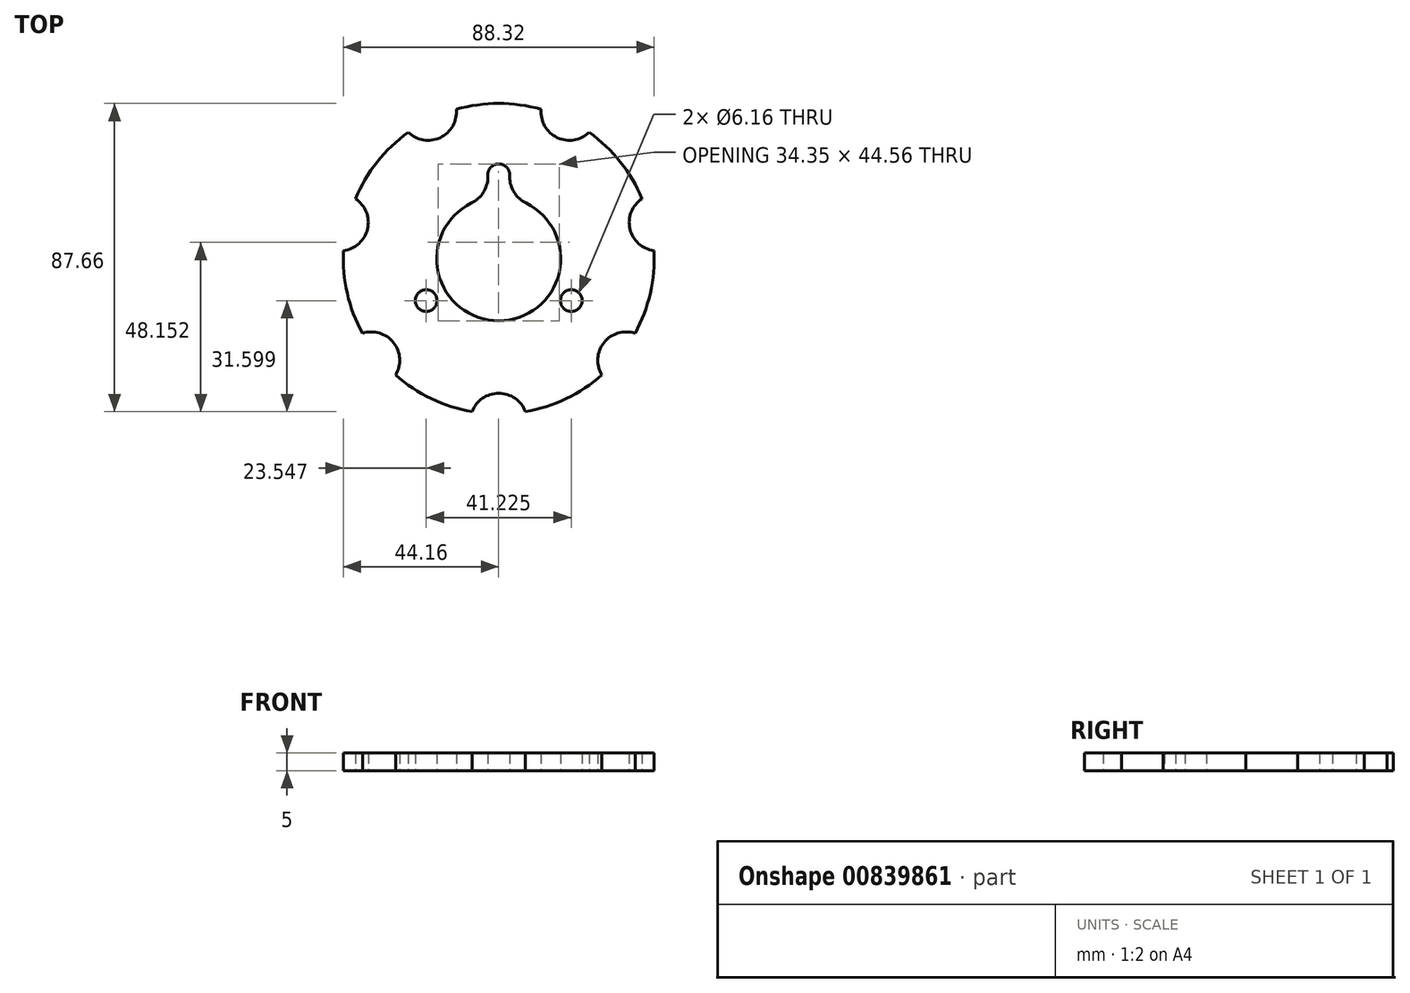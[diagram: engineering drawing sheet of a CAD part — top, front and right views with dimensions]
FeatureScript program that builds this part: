
annotation { "Feature Type Name" : "Feature", "Feature Type Description" : "" }
export const myFeature = defineFeature(function(context is Context, id is Id, definition is map)
    precondition{}
    {
        {
            var Q0;
            Q0=qCreatedBy(makeId("Top.planeOp"),FACE);
            var sketch = newSketch(context, id + "F0", { "sketchPlane" : qUnion([Q0])});
            skCircle(sketch, "E0", {"center": v(0, 0) * mm, "radius": 44.16 * mm});
            skCircle(sketch, "E1", {"center": v(0, 44.16) * mm, "radius": 12.16 * mm});
            skCircle(sketch, "E2.1.0", {"center": v(-34.52, 27.53) * mm, "radius": 12.16 * mm});
            skCircle(sketch, "E2.2.0", {"center": v(-43.05, -9.83) * mm, "radius": 12.16 * mm});
            skCircle(sketch, "E2.3.0", {"center": v(-19.16, -39.79) * mm, "radius": 12.16 * mm});
            skCircle(sketch, "E2.4.0", {"center": v(19.16, -39.79) * mm, "radius": 12.16 * mm});
            skCircle(sketch, "E2.5.0", {"center": v(43.05, -9.83) * mm, "radius": 12.16 * mm});
            skCircle(sketch, "E2.6.0", {"center": v(34.52, 27.53) * mm, "radius": 12.16 * mm});
            skCircle(sketch, "E3", {"center": v(20.1, 41.73) * mm, "radius": 8.08 * mm});
            skPoint(sketch, "E3.first.point", {"position": v(25.7, 35.9) * mm});
            skPoint(sketch, "E3.second.point", {"position": v(12.05, 42.48) * mm});
            skPoint(sketch, "E3.third.point", {"position": v(24.63, 48.42) * mm});
            skCircle(sketch, "E4.1.0", {"center": v(-20.1, 41.73) * mm, "radius": 8.08 * mm});
            skCircle(sketch, "E4.2.0", {"center": v(-45.16, 10.3) * mm, "radius": 8.08 * mm});
            skCircle(sketch, "E4.3.0", {"center": v(-36.21, -28.88) * mm, "radius": 8.08 * mm});
            skCircle(sketch, "E4.4.0", {"center": v(0, -46.32) * mm, "radius": 8.08 * mm});
            skCircle(sketch, "E4.5.0", {"center": v(36.21, -28.88) * mm, "radius": 8.08 * mm});
            skCircle(sketch, "E4.6.0", {"center": v(45.16, 10.3) * mm, "radius": 8.08 * mm});
            skCircle(sketch, "E5", {"center": v(0, 0) * mm, "radius": 17.63 * mm});
            skCircle(sketch, "E6", {"center": v(0, 23.8) * mm, "radius": 3.08 * mm});
            skCircle(sketch, "E7", {"center": v(0, 23.8) * mm, "radius": 3.13 * mm});
            skArc(sketch, "E8", {"start": v(-7.76, 15.83) * mm, "mid": v(-4.38, 18.85) * mm, "end": v(-3.07, 23.2) * mm});
            skArc(sketch, "E9.MirrorCS", {"start": v(7.76, 15.83) * mm, "mid": v(4.38, 18.85) * mm, "end": v(3.07, 23.2) * mm});
            skArc(sketch, "E10.1.0", {"start": v(-9.83, -14.64) * mm, "mid": v(-14.14, -13.22) * mm, "end": v(-18.55, -14.26) * mm});
            skCircle(sketch, "E10.1.1", {"center": v(-20.61, -11.9) * mm, "radius": 3.08 * mm});
            skArc(sketch, "E10.1.2", {"start": v(-17.59, -1.2) * mm, "mid": v(-18.52, -5.63) * mm, "end": v(-21.63, -8.94) * mm});
            skArc(sketch, "E10.2.0", {"start": v(17.59, -1.2) * mm, "mid": v(18.52, -5.63) * mm, "end": v(21.63, -8.94) * mm});
            skCircle(sketch, "E10.2.1", {"center": v(20.61, -11.9) * mm, "radius": 3.08 * mm});
            skArc(sketch, "E10.2.2", {"start": v(9.83, -14.64) * mm, "mid": v(14.14, -13.22) * mm, "end": v(18.55, -14.26) * mm});
            skSolve(sketch);
        }
        {
            var Q0;
            {var subQ1=sQuery(id+"F0.wireOp",EDGE,"E8");Q0=makeQuery(id+"F0.imprint","IMPRINT",FACE,{"disambiguationData":[TD([[makeQuery(id+"F0.imprint","IMPRINT",EDGE,{"derivedFrom":subQ1}),1.0]])]});}
            var Q1;
            {var subQ0=sQuery(id+"F0.wireOp",EDGE,"E2.1.0");var subQ1=sQuery(id+"F0.wireOp",EDGE,"E0");var subQ2=makeQuery(id+"F0.imprint","INTERSECT",VERTEX,{"derivedFrom":[subQ1,subQ0,sQuery(id+"F0.wireOp",EDGE,"E4.1.0")]});Q1=makeQuery(id+"F0.imprint","IMPRINT",FACE,{"disambiguationData":[TD([[makeQuery(id+"F0.imprint","IMPRINT",EDGE,{"disambiguationData":[TD([[subQ2,-1.0]])],"derivedFrom":subQ1}),1.0]])]});}
            var Q2;
            {var subQ0=sQuery(id+"F0.wireOp",EDGE,"E2.2.0");var subQ1=sQuery(id+"F0.wireOp",EDGE,"E0");var subQ2=makeQuery(id+"F0.imprint","INTERSECT",VERTEX,{"derivedFrom":[subQ1,subQ0,sQuery(id+"F0.wireOp",EDGE,"E4.2.0")]});Q2=makeQuery(id+"F0.imprint","IMPRINT",FACE,{"disambiguationData":[TD([[makeQuery(id+"F0.imprint","IMPRINT",EDGE,{"disambiguationData":[TD([[subQ2,-1.0]])],"derivedFrom":subQ1}),1.0]])]});}
            var Q3;
            {var subQ0=sQuery(id+"F0.wireOp",EDGE,"E2.3.0");var subQ1=sQuery(id+"F0.wireOp",EDGE,"E0");var subQ2=makeQuery(id+"F0.imprint","INTERSECT",VERTEX,{"derivedFrom":[subQ1,subQ0,sQuery(id+"F0.wireOp",EDGE,"E4.3.0")]});Q3=makeQuery(id+"F0.imprint","IMPRINT",FACE,{"disambiguationData":[TD([[makeQuery(id+"F0.imprint","IMPRINT",EDGE,{"disambiguationData":[TD([[subQ2,-1.0]])],"derivedFrom":subQ1}),1.0]])]});}
            var Q4;
            {var subQ0=sQuery(id+"F0.wireOp",EDGE,"E2.4.0");var subQ1=sQuery(id+"F0.wireOp",EDGE,"E0");var subQ2=makeQuery(id+"F0.imprint","INTERSECT",VERTEX,{"derivedFrom":[subQ1,subQ0,sQuery(id+"F0.wireOp",EDGE,"E4.4.0")]});Q4=makeQuery(id+"F0.imprint","IMPRINT",FACE,{"disambiguationData":[TD([[makeQuery(id+"F0.imprint","IMPRINT",EDGE,{"disambiguationData":[TD([[subQ2,-1.0]])],"derivedFrom":subQ1}),1.0]])]});}
            var Q5;
            {var subQ0=sQuery(id+"F0.wireOp",EDGE,"E2.5.0");var subQ1=sQuery(id+"F0.wireOp",EDGE,"E0");var subQ2=makeQuery(id+"F0.imprint","INTERSECT",VERTEX,{"derivedFrom":[subQ1,subQ0,sQuery(id+"F0.wireOp",EDGE,"E4.6.0")]});Q5=makeQuery(id+"F0.imprint","IMPRINT",FACE,{"disambiguationData":[TD([[makeQuery(id+"F0.imprint","IMPRINT",EDGE,{"disambiguationData":[TD([[subQ2,1.0]])],"derivedFrom":subQ1}),1.0]])]});}
            var Q6;
            {var subQ0=sQuery(id+"F0.wireOp",EDGE,"E2.6.0");var subQ1=sQuery(id+"F0.wireOp",EDGE,"E0");var subQ2=makeQuery(id+"F0.imprint","INTERSECT",VERTEX,{"derivedFrom":[subQ1,subQ0,sQuery(id+"F0.wireOp",EDGE,"E4.6.0")]});Q6=makeQuery(id+"F0.imprint","IMPRINT",FACE,{"disambiguationData":[TD([[makeQuery(id+"F0.imprint","IMPRINT",EDGE,{"disambiguationData":[TD([[subQ2,-1.0]])],"derivedFrom":subQ1}),1.0]])]});}
            var Q7;
            {var subQ0=sQuery(id+"F0.wireOp",EDGE,"E1");var subQ1=sQuery(id+"F0.wireOp",EDGE,"E0");var subQ2=makeQuery(id+"F0.imprint","INTERSECT",VERTEX,{"derivedFrom":[subQ1,subQ0,sQuery(id+"F0.wireOp",EDGE,"E3")]});Q7=makeQuery(id+"F0.imprint","IMPRINT",FACE,{"disambiguationData":[TD([[makeQuery(id+"F0.imprint","IMPRINT",EDGE,{"disambiguationData":[TD([[subQ2,-1.0]])],"derivedFrom":subQ1}),1.0]])]});}
            extrude(context, id + "F1", {"entities" : qUnion([Q0, Q1, Q2, Q3, Q4, Q5, Q6, Q7]), "depth" : 5 * mm, "offsetDistance" : 25 * mm});
        }
    });
